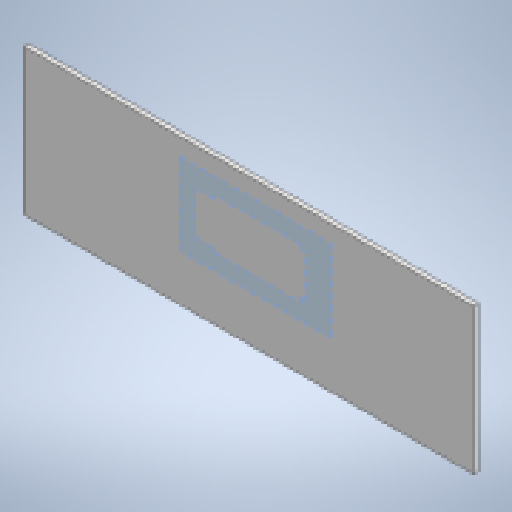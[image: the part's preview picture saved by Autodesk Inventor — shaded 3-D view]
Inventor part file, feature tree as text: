
AUTODESK INVENTOR PART (.ipt)
format: ipt  version: 2023 (Build 270158030, 158C)  size: 161,792 bytes
history: native  units: mm
features: reference x12, other x3, extrude x2, sketch x2, projected_geometry x1
ambient origin geometry x8: Origin, YZ Plane, XZ Plane, XY Plane, X Axis, Y Axis, Z Axis, Center Point
bodies: Solid1 (feature_tree)
feature tree (20):
  extrude  "Extrusion1"  Depth=15.0mm
  extrude  "Extrusion2"  Depth=3.0mm
  sketch  "Sketch1"  dims[d0=15.0mm d1=15.0mm]
  reference  "Reference1"
  reference  "Reference2"
  reference  "Reference3"
  reference  "Reference4"
  reference  "Reference5"
  reference  "Reference6"
  reference  "Reference7"
  reference  "Reference8"
  reference  "Reference9"
  reference  "Reference10"
  sketch  "Sketch2"  dims[d2=20.0mm d3=20.0mm d4=1.5mm d5=0.0mm d6=0.2mm d7=5.0mm d8=10.0mm d9=5.0mm d10=5.0mm d11=3.0mm d12=0.0mm]
  reference  "Reference11"
  projected_geometry  "Projected Loop1"
  reference  "Reference12"
  other  "<userpath>\Documents\0004-inventor\3D-CAD-main\cable-hanger\cable-hanger-hook.iam"
  other  "cable-hanger-hook.iam"
  other  "cable-hanger:1"
